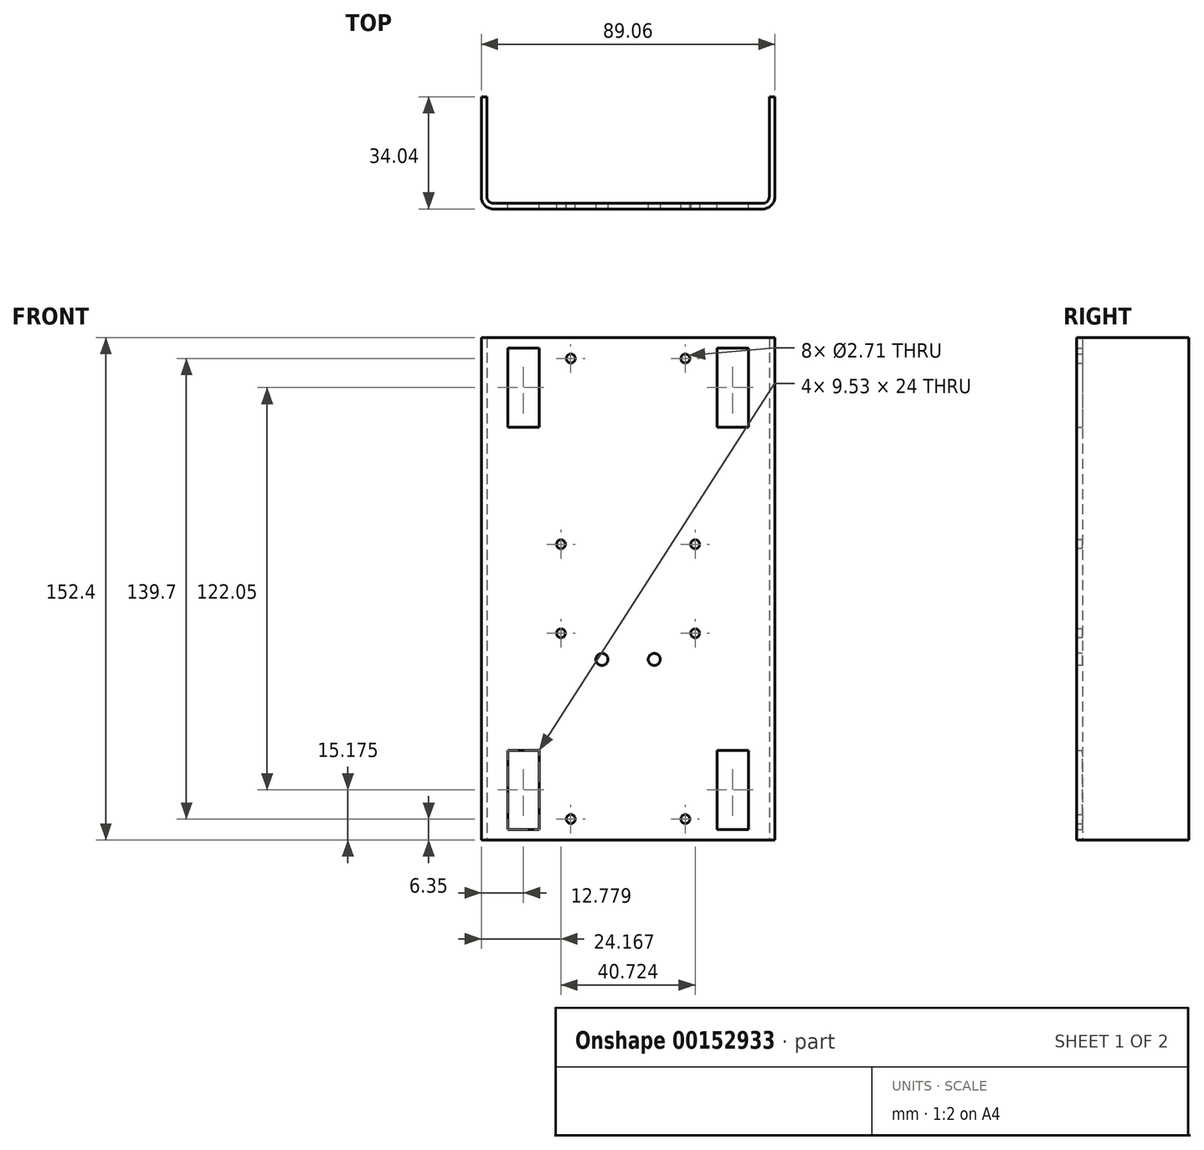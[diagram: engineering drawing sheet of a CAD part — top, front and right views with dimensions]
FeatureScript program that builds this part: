
annotation { "Feature Type Name" : "Feature", "Feature Type Description" : "" }
export const myFeature = defineFeature(function(context is Context, id is Id, definition is map)
    precondition{}
    {
        {
            var Q0;
            Q0=qCreatedBy(makeId("Top.planeOp"),FACE);
            var sketch = newSketch(context, id + "F0", { "sketchPlane" : qUnion([Q0])});
            skLineSegment(sketch, "E0.bottom", {"start": v(0, 0) * mm, "end": v(-85.64, 0) * mm});
            skLineSegment(sketch, "E0.top", {"start": v(1.7, -1.7) * mm, "end": v(-87.35, -1.7) * mm});
            skLineSegment(sketch, "E1.top", {"start": v(-85.64, 32.33) * mm, "end": v(-87.35, 32.33) * mm});
            skLineSegment(sketch, "E1.left", {"start": v(-85.64, 0) * mm, "end": v(-85.64, 32.33) * mm});
            skLineSegment(sketch, "E1.right", {"start": v(-87.35, -1.7) * mm, "end": v(-87.35, 32.33) * mm});
            skLineSegment(sketch, "E2.top", {"start": v(0, 32.33) * mm, "end": v(1.7, 32.33) * mm});
            skLineSegment(sketch, "E2.left", {"start": v(0, 0) * mm, "end": v(0, 32.33) * mm});
            skLineSegment(sketch, "E2.right", {"start": v(1.7, -1.7) * mm, "end": v(1.7, 32.33) * mm});
            skLineSegment(sketch, "E3", {"start": v(-42.82, 0) * mm, "end": v(-42.82, -1.7) * mm, "construction": true});
            skSolve(sketch);
        }
        {
            var Q0;
            Q0=qSketchRegion(id+"F0",true);
            extrude(context, id + "F1", {"entities" : qUnion([Q0]), "depth" : 152.4 * mm});
        }
        {
            var Q0;
            Q0=makeQuery(id+"FcdIcV9w6YY9zah_1.opExtrude","CAP_EDGE",EDGE,{"disambiguationData":[OSD([sQuery(id+"FU7sgaIbCbRhSfr_1.wireOp",EDGE,"F29Sxc5V-O2cl-wjtz-gx5o-reTTBG7m1pNU.top")])],"isStart":true});
            var Q1;
            Q1=makeQuery(id+"FcdIcV9w6YY9zah_1.opExtrude","CAP_EDGE",EDGE,{"disambiguationData":[OSD([sQuery(id+"FU7sgaIbCbRhSfr_1.wireOp",EDGE,"yv2bQU74-Eht6-uYuo-WBF2-3C4kyuaz0slr.top")])],"isStart":true});
            var Q2;
            Q2=makeQuery(id+"F1.opExtrude","SWEPT_EDGE",EDGE,{"disambiguationData":[OSD([sQuery(id+"F0.wireOp",EDGE,"E0.bottom"),sQuery(id+"F0.wireOp",EDGE,"E2.left")])]});
            var Q3;
            Q3=makeQuery(id+"F1.opExtrude","SWEPT_EDGE",EDGE,{"disambiguationData":[OSD([sQuery(id+"F0.wireOp",EDGE,"E0.bottom"),sQuery(id+"F0.wireOp",EDGE,"E1.left")])]});
            fillet(context, id + "F2", {"entities" : qUnion([Q0, Q1, Q2, Q3]), "radius" : 1.98 * mm, "tangentPropagation" : true, "allowEdgeOverflow" : false});
        }
        {
            var Q0;
            Q0=makeQuery(id+"FkwQQH4eT4IjhdK_1.opExtrude","CAP_EDGE",EDGE,{"disambiguationData":[OSD([sQuery(id+"FvDFSbhwMPyTNrQ_1.wireOp",EDGE,"223FG13h-YrEq-unoX-9EOi-DwKLLmwbrteD.top")])],"isStart":false});
            var Q1;
            Q1=makeQuery(id+"F1.opExtrude","SWEPT_EDGE",EDGE,{"disambiguationData":[OSD([sQuery(id+"F0.wireOp",EDGE,"E0.top"),sQuery(id+"F0.wireOp",EDGE,"E2.right")])]});
            var Q2;
            Q2=makeQuery(id+"F1.opExtrude","SWEPT_EDGE",EDGE,{"disambiguationData":[OSD([sQuery(id+"F0.wireOp",EDGE,"E0.top"),sQuery(id+"F0.wireOp",EDGE,"E1.right")])]});
            var Q3;
            Q3=makeQuery(id+"F2kHonbXZaQoFrR_1.opExtrude","CAP_EDGE",EDGE,{"disambiguationData":[OSD([sQuery(id+"FsAbJG8AZOSwdHE_1.wireOp",EDGE,"WRaIy3id-o2EU-qHqw-IwdC-eHQZRSiK4KpF.bottom")])],"isStart":false});
            fillet(context, id + "F3", {"entities" : qUnion([Q0, Q1, Q2, Q3]), "radius" : 3.7 * mm, "tangentPropagation" : true, "allowEdgeOverflow" : false});
        }
        {
            var Q0;
            Q0=makeQuery(id+"F1.opExtrude","SWEPT_FACE",FACE,{"disambiguationData":[OSD([sQuery(id+"F0.wireOp",EDGE,"E0.bottom")])]});
            var sketch = newSketch(context, id + "F4", { "sketchPlane" : qUnion([Q0])});
            skLineSegment(sketch, "E4", {"start": v(42.82, 0) * mm, "end": v(42.82, 152.4) * mm, "construction": true});
            skLineSegment(sketch, "E5.bottom", {"start": v(83.66, 0) * mm, "end": v(74.57, 0) * mm, "construction": true});
            skLineSegment(sketch, "E5.top", {"start": v(83.66, 15.17) * mm, "end": v(74.57, 15.17) * mm, "construction": true});
            skLineSegment(sketch, "E5.left", {"start": v(83.66, 0) * mm, "end": v(83.66, 15.17) * mm, "construction": true});
            skLineSegment(sketch, "E5.right", {"start": v(74.57, 0) * mm, "end": v(74.57, 15.17) * mm, "construction": true});
            skLineSegment(sketch, "E6.bottom", {"start": v(74.57, 15.18) * mm, "end": v(11.07, 15.18) * mm, "construction": true});
            skLineSegment(sketch, "E6.top", {"start": v(74.57, 137.22) * mm, "end": v(11.07, 137.22) * mm, "construction": true});
            skLineSegment(sketch, "E6.left", {"start": v(74.57, 15.17) * mm, "end": v(74.57, 137.23) * mm, "construction": true});
            skLineSegment(sketch, "E6.right", {"start": v(11.07, 15.18) * mm, "end": v(11.07, 137.22) * mm, "construction": true});
            skPoint(sketch, "E6.middle", {"position": v(42.82, 76.2) * mm});
            skLineSegment(sketch, "E7.bottom", {"start": v(69.8, 3.18) * mm, "end": v(79.34, 3.18) * mm});
            skLineSegment(sketch, "E7.top", {"start": v(69.8, 27.18) * mm, "end": v(79.34, 27.18) * mm});
            skLineSegment(sketch, "E7.left", {"start": v(69.8, 3.17) * mm, "end": v(69.8, 27.18) * mm});
            skLineSegment(sketch, "E7.right", {"start": v(79.34, 3.17) * mm, "end": v(79.34, 27.18) * mm});
            skPoint(sketch, "E7.middle", {"position": v(74.57, 15.17) * mm});
            skLineSegment(sketch, "E8.bottom", {"start": v(15.84, 3.18) * mm, "end": v(6.3, 3.18) * mm});
            skLineSegment(sketch, "E8.top", {"start": v(15.84, 27.18) * mm, "end": v(6.3, 27.18) * mm});
            skLineSegment(sketch, "E8.left", {"start": v(15.84, 3.18) * mm, "end": v(15.84, 27.18) * mm});
            skLineSegment(sketch, "E8.right", {"start": v(6.3, 3.18) * mm, "end": v(6.3, 27.18) * mm});
            skPoint(sketch, "E8.middle", {"position": v(11.07, 15.18) * mm});
            skLineSegment(sketch, "E9.bottom", {"start": v(6.3, 149.22) * mm, "end": v(15.84, 149.22) * mm});
            skLineSegment(sketch, "E9.top", {"start": v(6.3, 125.22) * mm, "end": v(15.84, 125.22) * mm});
            skLineSegment(sketch, "E9.left", {"start": v(6.3, 149.22) * mm, "end": v(6.3, 125.22) * mm});
            skLineSegment(sketch, "E9.right", {"start": v(15.84, 149.22) * mm, "end": v(15.84, 125.22) * mm});
            skPoint(sketch, "E9.middle", {"position": v(11.07, 137.22) * mm});
            skLineSegment(sketch, "E10.bottom", {"start": v(69.8, 149.23) * mm, "end": v(79.34, 149.23) * mm});
            skLineSegment(sketch, "E10.top", {"start": v(69.8, 125.23) * mm, "end": v(79.34, 125.23) * mm});
            skLineSegment(sketch, "E10.left", {"start": v(69.8, 149.23) * mm, "end": v(69.8, 125.23) * mm});
            skLineSegment(sketch, "E10.right", {"start": v(79.34, 149.23) * mm, "end": v(79.34, 125.23) * mm});
            skPoint(sketch, "E10.middle", {"position": v(74.57, 137.23) * mm});
            skLineSegment(sketch, "E11.bottom", {"start": v(60.2, 6.35) * mm, "end": v(25.44, 6.35) * mm, "construction": true});
            skLineSegment(sketch, "E11.top", {"start": v(60.2, 146.05) * mm, "end": v(25.44, 146.05) * mm, "construction": true});
            skLineSegment(sketch, "E11.left", {"start": v(60.2, 6.35) * mm, "end": v(60.2, 146.05) * mm, "construction": true});
            skLineSegment(sketch, "E11.right", {"start": v(25.44, 6.35) * mm, "end": v(25.44, 146.05) * mm, "construction": true});
            skLineSegment(sketch, "E12", {"start": v(69.8, 3.18) * mm, "end": v(60.2, 3.18) * mm, "construction": true});
            skLineSegment(sketch, "E13", {"start": v(60.2, 3.18) * mm, "end": v(60.2, 6.35) * mm, "construction": true});
            skCircle(sketch, "E14", {"center": v(60.2, 6.35) * mm, "radius": 1.35 * mm});
            skCircle(sketch, "E15", {"center": v(25.44, 6.35) * mm, "radius": 1.35 * mm});
            skCircle(sketch, "E16", {"center": v(25.44, 146.05) * mm, "radius": 1.35 * mm});
            skCircle(sketch, "E17", {"center": v(60.2, 146.05) * mm, "radius": 1.35 * mm});
            skSolve(sketch);
        }
        {
            var Q0;
            Q0=qSketchRegion(id+"F4",true);
            var Q1;
            Q1=makeQuery(id+"F1.opExtrude","SWEPT_FACE",FACE,{"disambiguationData":[OSD([sQuery(id+"F0.wireOp",EDGE,"E0.top")])]});
            extrude(context, id + "F5", {"entities" : qUnion([Q0]), "operationType" : NewBodyOperationType.REMOVE, "endBound" : BoundingType.UP_TO_SURFACE, "oppositeDirection" : true, "endBoundEntityFace" : qUnion([Q1]), "depth" : 25.4 * mm});
        }
        {
            var Q0;
            Q0=makeQuery(id+"F1.opExtrude","SWEPT_FACE",FACE,{"disambiguationData":[OSD([sQuery(id+"F0.wireOp",EDGE,"E0.top")])]});
            var sketch = newSketch(context, id + "F6", { "sketchPlane" : qUnion([Q0])});
            skLineSegment(sketch, "E18", {"start": v(-42.82, 152.4) * mm, "end": v(-42.82, 76.53) * mm, "construction": true});
            skLineSegment(sketch, "E19.bottom", {"start": v(-22.46, 89.7) * mm, "end": v(-63.18, 89.7) * mm, "construction": true});
            skLineSegment(sketch, "E19.top", {"start": v(-22.46, 62.7) * mm, "end": v(-63.18, 62.7) * mm, "construction": true});
            skLineSegment(sketch, "E19.left", {"start": v(-22.46, 89.7) * mm, "end": v(-22.46, 62.7) * mm, "construction": true});
            skLineSegment(sketch, "E19.right", {"start": v(-63.18, 89.7) * mm, "end": v(-63.18, 62.7) * mm, "construction": true});
            skPoint(sketch, "E19.middle", {"position": v(-42.82, 76.2) * mm});
            skCircle(sketch, "E20", {"center": v(-63.18, 89.7) * mm, "radius": 1.35 * mm});
            skCircle(sketch, "E21", {"center": v(-22.46, 89.7) * mm, "radius": 1.35 * mm});
            skCircle(sketch, "E22", {"center": v(-22.46, 62.7) * mm, "radius": 1.35 * mm});
            skCircle(sketch, "E23", {"center": v(-63.18, 62.7) * mm, "radius": 1.35 * mm});
            skLineSegment(sketch, "E24", {"start": v(-42.82, 76.2) * mm, "end": v(-42.82, 54.77) * mm, "construction": true});
            skLineSegment(sketch, "E25", {"start": v(-42.82, 54.77) * mm, "end": v(-42.82, 0) * mm, "construction": true});
            skLineSegment(sketch, "E26", {"start": v(-83.66, 76.2) * mm, "end": v(-1.98, 76.2) * mm, "construction": true});
            skLineSegment(sketch, "E27", {"start": v(-50.76, 54.77) * mm, "end": v(-34.88, 54.77) * mm, "construction": true});
            skCircle(sketch, "E28", {"center": v(-50.76, 54.77) * mm, "radius": 1.83 * mm});
            skCircle(sketch, "E29", {"center": v(-34.88, 54.77) * mm, "radius": 1.83 * mm});
            skSolve(sketch);
        }
        {
            var Q0;
            Q0 = qSketchRegion(id + "F6", true);
            var Q1;
            Q1=makeQuery(id+"F1.opExtrude","SWEPT_FACE",FACE,{"disambiguationData":[OSD([sQuery(id+"F0.wireOp",EDGE,"E0.bottom")])]});
            extrude(context, id + "F7", {"entities" : qUnion([Q0]), "operationType" : NewBodyOperationType.REMOVE, "endBound" : BoundingType.UP_TO_SURFACE, "oppositeDirection" : true, "endBoundEntityFace" : qUnion([Q1]), "depth" : 25.4 * mm});
        }
    });
